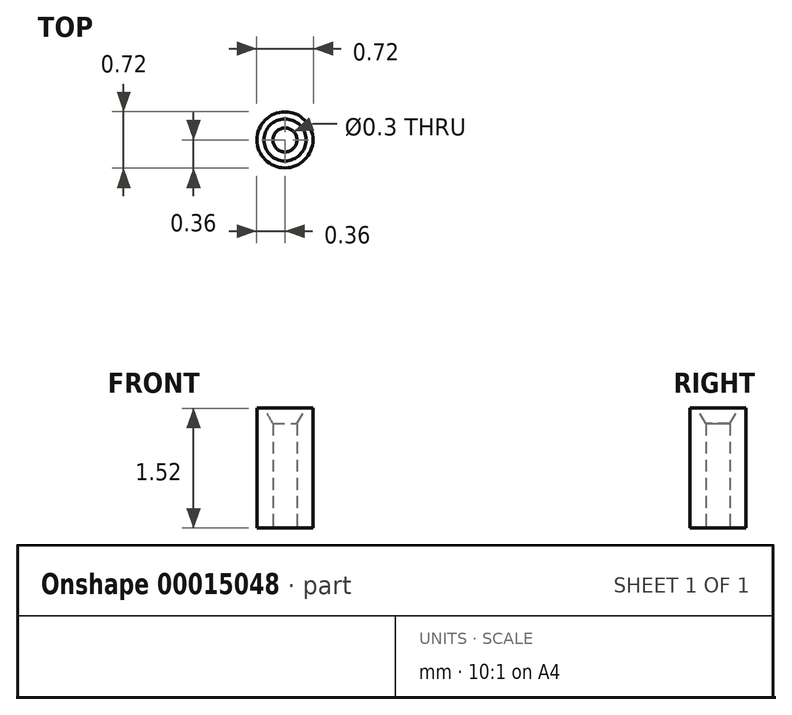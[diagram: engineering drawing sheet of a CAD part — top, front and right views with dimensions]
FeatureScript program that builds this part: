
annotation { "Feature Type Name" : "Feature", "Feature Type Description" : "" }
export const myFeature = defineFeature(function(context is Context, id is Id, definition is map)
    precondition{}
    {
        {
            var Q0;
            Q0=qCreatedBy(makeId("Front.planeOp"),FACE);
            var sketch = newSketch(context, id + "F0", { "sketchPlane" : qUnion([Q0])});
            skLineSegment(sketch, "E0", {"start": v(0.15, 0) * mm, "end": v(0.15, 1.33) * mm});
            skLineSegment(sketch, "E1", {"start": v(0.15, 1.33) * mm, "end": v(0.27, 1.52) * mm});
            skLineSegment(sketch, "E2", {"start": v(0.27, 1.52) * mm, "end": v(0.36, 1.52) * mm});
            skLineSegment(sketch, "E3", {"start": v(0.36, 1.52) * mm, "end": v(0.36, 0) * mm});
            skLineSegment(sketch, "E4", {"start": v(0.36, 0) * mm, "end": v(0.15, 0) * mm});
            skLineSegment(sketch, "E5", {"start": v(0, 0) * mm, "end": v(0, 1.52) * mm, "construction": true});
            skSolve(sketch);
        }
        {
            var Q0;
            Q0 = qSketchRegion(id + "F0", true);
            var Q1;
            Q1=sQuery(id+"F0.wireOp",EDGE,"E5");
            revolve(context, id + "F1", {"entities" : qUnion([Q0]), "axis" : qUnion([Q1]), "revolveType" : RevolveType.FULL});
        }
    });
